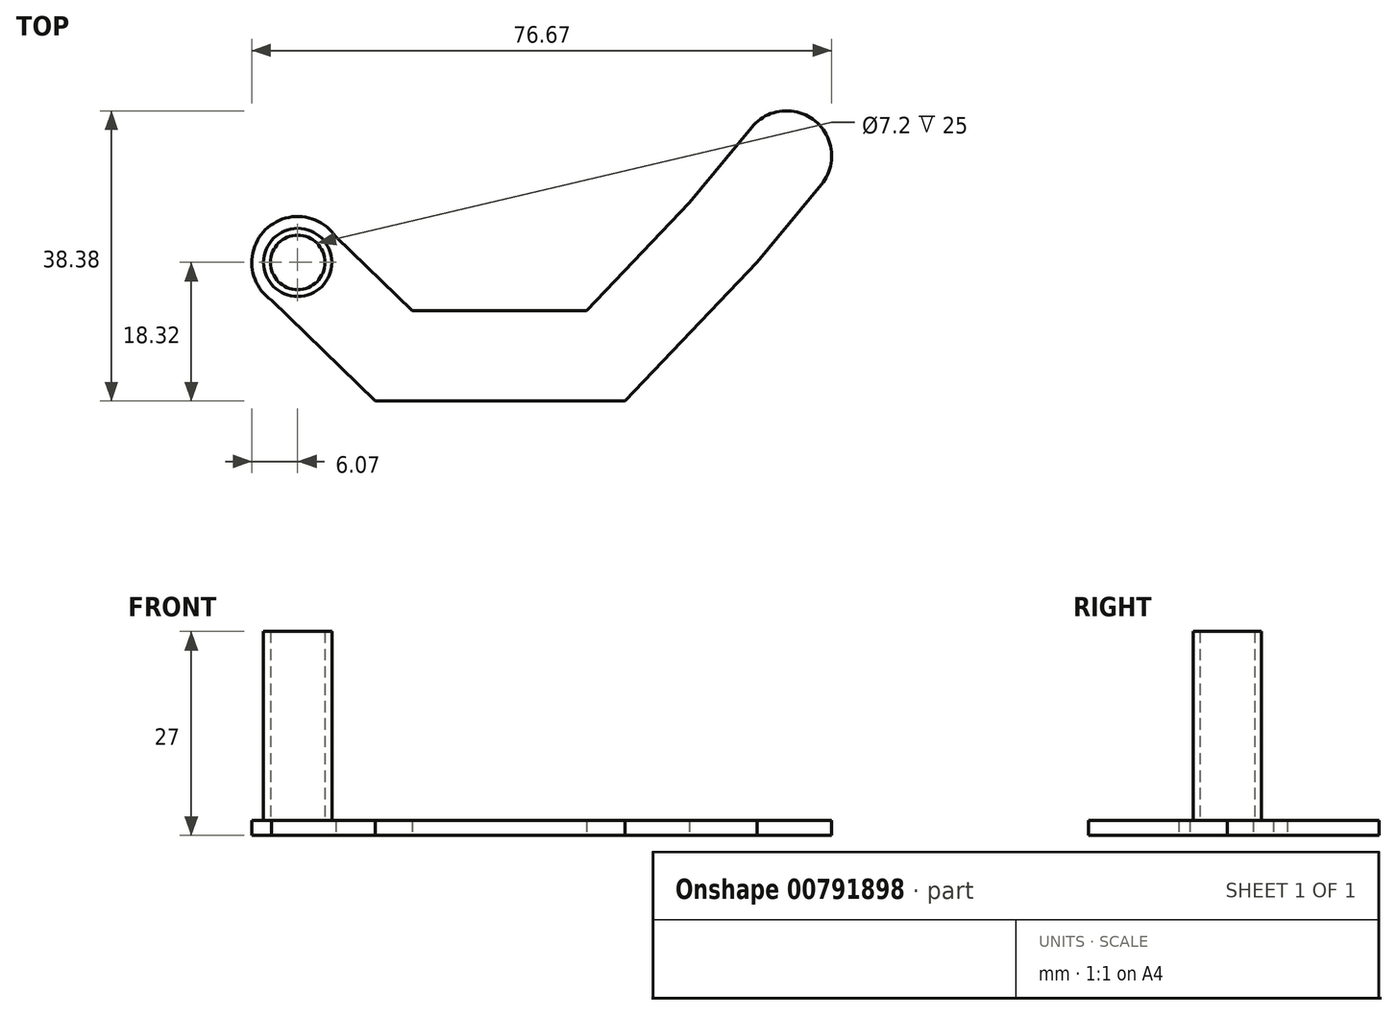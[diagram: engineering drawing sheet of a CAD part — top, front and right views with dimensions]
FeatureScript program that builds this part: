
annotation { "Feature Type Name" : "Feature", "Feature Type Description" : "" }
export const myFeature = defineFeature(function(context is Context, id is Id, definition is map)
    precondition{}
    {
        {
            var Q0;
            Q0=qCreatedBy(makeId("Top.planeOp"),FACE);
            var sketch = newSketch(context, id + "F0", { "sketchPlane" : qUnion([Q0])});
            skCircle(sketch, "E0", {"center": v(0, 0) * mm, "radius": 3.6 * mm});
            skArc(sketch, "E1", {"start": v(5.03, 3.4) * mm, "mid": v(-4.26, 4.32) * mm, "end": v(-3.48, -4.98) * mm});
            skLineSegment(sketch, "E2", {"start": v(-3.48, -4.98) * mm, "end": v(10.28, -18.32) * mm});
            skLineSegment(sketch, "E3", {"start": v(10.28, -18.32) * mm, "end": v(43.3, -18.32) * mm});
            skLineSegment(sketch, "E4", {"start": v(43.3, -18.32) * mm, "end": v(60.75, 0) * mm});
            skLineSegment(sketch, "E5", {"start": v(60.75, 0) * mm, "end": v(69.24, 10.3) * mm});
            skLineSegment(sketch, "E6.0", {"start": v(51.81, 7.93) * mm, "end": v(60.03, 17.89) * mm});
            skLineSegment(sketch, "E6.1", {"start": v(38.18, -6.39) * mm, "end": v(51.81, 7.93) * mm});
            skLineSegment(sketch, "E6.2", {"start": v(15.12, -6.39) * mm, "end": v(38.18, -6.39) * mm});
            skLineSegment(sketch, "E6.3", {"start": v(5.03, 3.4) * mm, "end": v(15.12, -6.39) * mm});
            skArc(sketch, "E7", {"start": v(69.24, 10.3) * mm, "mid": v(68.43, 18.7) * mm, "end": v(60.03, 17.89) * mm});
            skCircle(sketch, "E8", {"center": v(0, 0) * mm, "radius": 4.5 * mm});
            skSolve(sketch);
        }
        {
            var Q0;
            Q0=makeQuery(id+"F0.imprint","IMPRINT",FACE,{"disambiguationData":[TD([[makeQuery(id+"F0.imprint","IMPRINT",EDGE,{"derivedFrom":sQuery(id+"F0.wireOp",EDGE,"E1")}),1.0]])]});
            var Q1;
            Q1=makeQuery(id+"F0.imprint","IMPRINT",FACE,{"disambiguationData":[TD([[makeQuery(id+"F0.imprint","IMPRINT",EDGE,{"derivedFrom":sQuery(id+"F0.wireOp",EDGE,"E0")}),1.0]])]});
            var Q2;
            Q2=makeQuery(id+"F0.imprint","IMPRINT",FACE,{"disambiguationData":[TD([[makeQuery(id+"F0.imprint","IMPRINT",EDGE,{"derivedFrom":sQuery(id+"F0.wireOp",EDGE,"E0")}),-1.0]])]});
            extrude(context, id + "F1", {"entities" : qUnion([Q0, Q1, Q2]), "depth" : 2 * mm, "offsetDistance" : 25.4 * mm});
        }
        {
            var Q0;
            Q0=makeQuery(id+"F1.opExtrude","CAP_FACE",FACE,{"disambiguationData":[OSD([sQuery(id+"F0.wireOp",EDGE,"E1"),sQuery(id+"F0.wireOp",EDGE,"E2"),sQuery(id+"F0.wireOp",EDGE,"E3"),sQuery(id+"F0.wireOp",EDGE,"E4"),sQuery(id+"F0.wireOp",EDGE,"E5"),sQuery(id+"F0.wireOp",EDGE,"E6.0"),sQuery(id+"F0.wireOp",EDGE,"E6.1"),sQuery(id+"F0.wireOp",EDGE,"E6.2"),sQuery(id+"F0.wireOp",EDGE,"E6.3"),sQuery(id+"F0.wireOp",EDGE,"E7")])],"isStart":false});
            var sketch = newSketch(context, id + "F2", { "sketchPlane" : qUnion([Q0])});
            skCircle(sketch, "E9", {"center": v(0, 0) * mm, "radius": 3.6 * mm});
            skCircle(sketch, "E10", {"center": v(0, 0) * mm, "radius": 4.5 * mm});
            skSolve(sketch);
        }
        {
            var Q0;
            Q0=makeQuery(id+"F2.imprint","IMPRINT",FACE,{"disambiguationData":[TD([[makeQuery(id+"F2.imprint","IMPRINT",EDGE,{"derivedFrom":sQuery(id+"F2.wireOp",EDGE,"E9")}),-1.0]])]});
            extrude(context, id + "F3", {"entities" : qUnion([Q0]), "operationType" : NewBodyOperationType.ADD, "depth" : 25 * mm, "offsetDistance" : 25.4 * mm});
        }
    });
